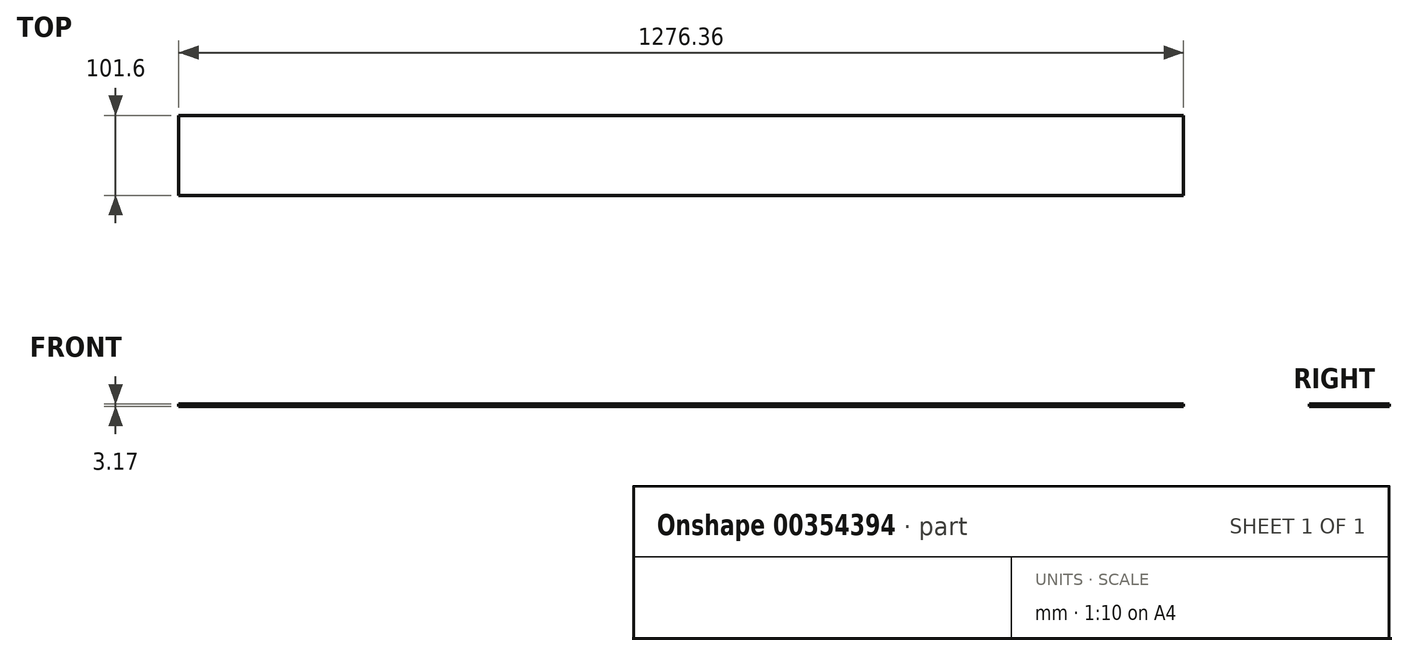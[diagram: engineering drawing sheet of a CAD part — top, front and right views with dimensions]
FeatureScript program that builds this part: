
annotation { "Feature Type Name" : "Feature", "Feature Type Description" : "" }
export const myFeature = defineFeature(function(context is Context, id is Id, definition is map)
    precondition{}
    {
        {
            var Q0;
            Q0=qCreatedBy(makeId("Top.planeOp"),FACE);
            var sketch = newSketch(context, id + "F0", { "sketchPlane" : qUnion([Q0])});
            skLineSegment(sketch, "E0.bottom", {"start": v(638.18, 50.8) * mm, "end": v(-638.18, 50.8) * mm});
            skLineSegment(sketch, "E0.top", {"start": v(638.18, -50.8) * mm, "end": v(-638.18, -50.8) * mm});
            skLineSegment(sketch, "E0.left", {"start": v(638.18, 50.8) * mm, "end": v(638.18, -50.8) * mm});
            skLineSegment(sketch, "E0.right", {"start": v(-638.18, 50.8) * mm, "end": v(-638.18, -50.8) * mm});
            skPoint(sketch, "E0.middle", {"position": v(0, 0) * mm});
            skSolve(sketch);
        }
        {
            var Q0;
            Q0 = qSketchRegion(id + "F0", true);
            extrude(context, id + "F1", {"entities" : qUnion([Q0]), "depth" : 3.17 * mm});
        }
    });
